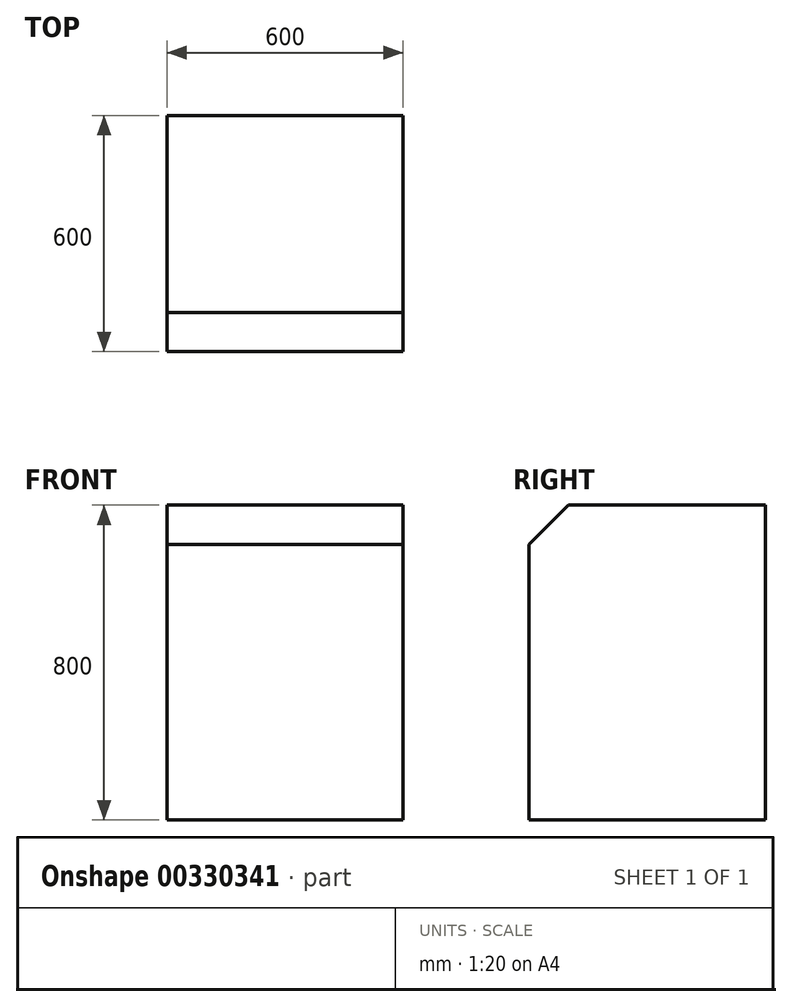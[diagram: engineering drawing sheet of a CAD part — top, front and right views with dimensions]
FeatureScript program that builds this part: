
annotation { "Feature Type Name" : "Feature", "Feature Type Description" : "" }
export const myFeature = defineFeature(function(context is Context, id is Id, definition is map)
    precondition{}
    {
        {
            var Q0;
            Q0=qCreatedBy(makeId("Right.planeOp"),FACE);
            var sketch = newSketch(context, id + "F0", { "sketchPlane" : qUnion([Q0])});
            skLineSegment(sketch, "E0", {"start": v(0, 0) * mm, "end": v(-600, 0) * mm});
            skLineSegment(sketch, "E1", {"start": v(-600, 0) * mm, "end": v(-600, 700) * mm});
            skLineSegment(sketch, "E2", {"start": v(-600, 700) * mm, "end": v(-500, 800) * mm});
            skLineSegment(sketch, "E3", {"start": v(-500, 800) * mm, "end": v(0, 800) * mm});
            skLineSegment(sketch, "E4", {"start": v(0, 800) * mm, "end": v(0, 0) * mm});
            skSolve(sketch);
        }
        {
            var Q0;
            Q0=qSketchRegion(id+"F0",true);
            extrude(context, id + "F1", {"entities" : qUnion([Q0]), "depth" : 600 * mm});
        }
    });
